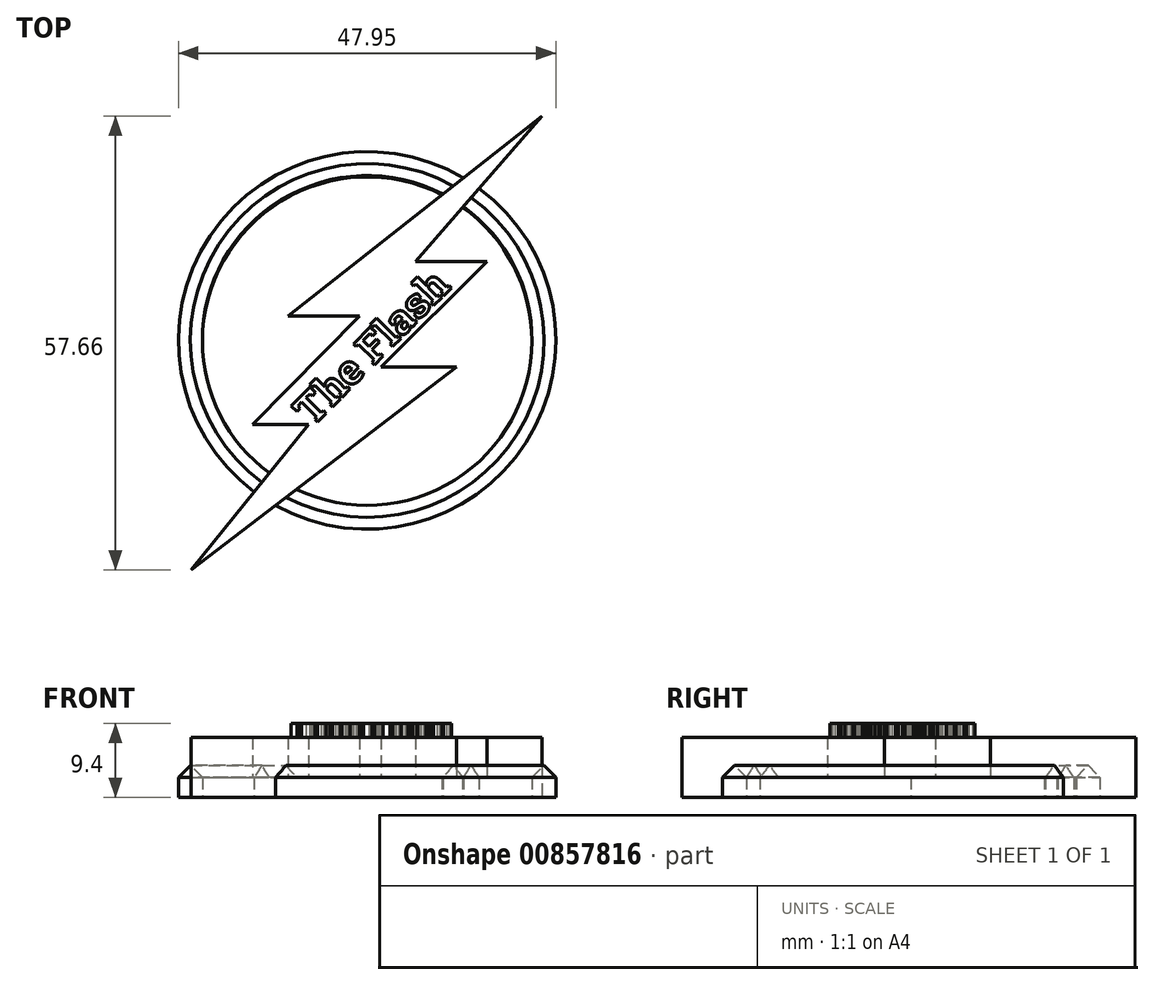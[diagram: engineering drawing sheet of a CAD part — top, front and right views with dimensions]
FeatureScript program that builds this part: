
annotation { "Feature Type Name" : "Feature", "Feature Type Description" : "" }
export const myFeature = defineFeature(function(context is Context, id is Id, definition is map)
    precondition{}
    {
        {
            var Q0;
            Q0=qCreatedBy(makeId("Top.planeOp"),FACE);
            var sketch = newSketch(context, id + "F0", { "sketchPlane" : qUnion([Q0])});
            skCircle(sketch, "E0", {"center": v(35.07, 35.87) * mm, "radius": 20.94 * mm});
            skCircle(sketch, "E1", {"center": v(35.07, 35.87) * mm, "radius": 23.98 * mm});
            skSolve(sketch);
        }
        {
            var Q0;
            Q0=qCreatedBy(makeId("Top.planeOp"),FACE);
            var sketch = newSketch(context, id + "F1", { "sketchPlane" : qUnion([Q0])});
            skLineSegment(sketch, "E2", {"start": v(57.25, 64.38) * mm, "end": v(25.02, 38.95) * mm});
            skLineSegment(sketch, "E3", {"start": v(25.02, 38.95) * mm, "end": v(34.1, 38.95) * mm});
            skLineSegment(sketch, "E4", {"start": v(34.1, 38.95) * mm, "end": v(20.49, 25.19) * mm});
            skLineSegment(sketch, "E5", {"start": v(20.49, 25.19) * mm, "end": v(27.61, 25.19) * mm});
            skLineSegment(sketch, "E6", {"start": v(27.61, 25.19) * mm, "end": v(12.71, 6.72) * mm});
            skLineSegment(sketch, "E7", {"start": v(12.71, 6.72) * mm, "end": v(46.4, 32.47) * mm});
            skLineSegment(sketch, "E8", {"start": v(46.4, 32.47) * mm, "end": v(36.85, 32.47) * mm});
            skLineSegment(sketch, "E9", {"start": v(36.85, 32.47) * mm, "end": v(50.29, 45.92) * mm});
            skLineSegment(sketch, "E10", {"start": v(50.29, 45.92) * mm, "end": v(41.22, 45.92) * mm});
            skLineSegment(sketch, "E11", {"start": v(41.22, 45.92) * mm, "end": v(57.25, 64.38) * mm});
            skSolve(sketch);
        }
        {
            var Q0;
            Q0=makeQuery(id+"F1.imprint","IMPRINT",FACE,{"disambiguationData":[TD([[makeQuery(id+"F1.imprint","IMPRINT",EDGE,{"derivedFrom":sQuery(id+"F1.wireOp",EDGE,"E2")}),1.0]])]});
            extrude(context, id + "F2", {"entities" : qUnion([Q0]), "depth" : 7.62 * mm, "offsetDistance" : 25.4 * mm});
        }
        {
            var Q0;
            Q0=makeQuery(id+"F0.imprint","IMPRINT",FACE,{"disambiguationData":[TD([[makeQuery(id+"F0.imprint","IMPRINT",EDGE,{"derivedFrom":sQuery(id+"F0.wireOp",EDGE,"E0")}),-1.0]])]});
            extrude(context, id + "F3", {"entities" : qUnion([Q0]), "operationType" : NewBodyOperationType.ADD, "depth" : 5.08 * mm, "offsetDistance" : 25.4 * mm});
        }
        {
            var Q0;
            Q0=qCreatedBy(makeId("Top.planeOp"),FACE);
            var sketch = newSketch(context, id + "F4", { "sketchPlane" : qUnion([Q0])});
            skCircle(sketch, "E12", {"center": v(35.07, 35.71) * mm, "radius": 20.94 * mm});
            skSolve(sketch);
        }
        {
            var Q0;
            Q0 = qSketchRegion(id + "F4", true);
            extrude(context, id + "F5", {"entities" : qUnion([Q0]), "operationType" : NewBodyOperationType.ADD, "depth" : 2.54 * mm, "offsetDistance" : 25.4 * mm});
        }
        {
            var Q0;
            Q0=qCreatedBy(makeId("Top.planeOp"),FACE);
            var sketch = newSketch(context, id + "F6", { "sketchPlane" : qUnion([Q0])});
            skText(sketch, "E13", { "text": "The Flash", "fontName": "RobotoSlab-Bold.ttf"});
            const initialGuessF6  = {"E13": [0.02803, 0.0248, 0.7071, 0.7071, 0.00384]};
            skSetInitialGuess(sketch, initialGuessF6);
            skSolve(sketch);
        }
        {
            var Q0;
            Q0 = qSketchRegion(id + "F6", true);
            extrude(context, id + "F7", {"entities" : qUnion([Q0]), "operationType" : NewBodyOperationType.ADD, "depth" : 9.4 * mm, "offsetDistance" : 25.4 * mm});
        }
        {
            var Q0;
            {var subQ0=sQuery(id+"F0.wireOp",EDGE,"E0");Q0=makeQuery(id+"F3.boolean.opBoolean","SPLIT",EDGE,{"disambiguationData":[TD([makeQuery(id+"F2.opExtrude","SWEPT_FACE",FACE,{"disambiguationData":[OSD([sQuery(id+"F1.wireOp",EDGE,"E2")])]})])],"derivedFrom":makeQuery(id+"F3.opExtrude","CAP_EDGE",EDGE,{"disambiguationData":[OSD([subQ0])],"isStart":false})});}
            var Q1;
            {var subQ0=sQuery(id+"F0.wireOp",EDGE,"E1");Q1=makeQuery(id+"F3.boolean.opBoolean","SPLIT",EDGE,{"disambiguationData":[TD([makeQuery(id+"F2.opExtrude","SWEPT_FACE",FACE,{"disambiguationData":[OSD([sQuery(id+"F1.wireOp",EDGE,"E2")])]})])],"derivedFrom":makeQuery(id+"F3.opExtrude","CAP_EDGE",EDGE,{"disambiguationData":[OSD([subQ0])],"isStart":false})});}
            var Q2;
            {var subQ0=sQuery(id+"F0.wireOp",EDGE,"E1");Q2=makeQuery(id+"F3.boolean.opBoolean","SPLIT",EDGE,{"disambiguationData":[TD([makeQuery(id+"F2.opExtrude","SWEPT_FACE",FACE,{"disambiguationData":[OSD([sQuery(id+"F1.wireOp",EDGE,"E7")])]})])],"derivedFrom":makeQuery(id+"F3.opExtrude","CAP_EDGE",EDGE,{"disambiguationData":[OSD([subQ0])],"isStart":false})});}
            var Q3;
            {var subQ0=sQuery(id+"F0.wireOp",EDGE,"E0");Q3=makeQuery(id+"F3.boolean.opBoolean","SPLIT",EDGE,{"disambiguationData":[TD([makeQuery(id+"F2.opExtrude","SWEPT_FACE",FACE,{"disambiguationData":[OSD([sQuery(id+"F1.wireOp",EDGE,"E7")])]})])],"derivedFrom":makeQuery(id+"F3.opExtrude","CAP_EDGE",EDGE,{"disambiguationData":[OSD([subQ0])],"isStart":false})});}
            chamfer(context, id + "F8", {"entities" : qUnion([Q0, Q1, Q2, Q3]), "width" : 2.54 * mm, "tangentPropagation" : true});
        }
    });
